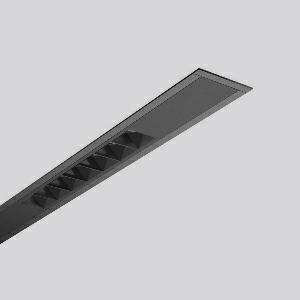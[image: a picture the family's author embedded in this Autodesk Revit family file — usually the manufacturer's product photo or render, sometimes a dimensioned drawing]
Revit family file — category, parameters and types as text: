
# Revit family: less_is_more_beamline_312467_003_1_76_66ad
name_source: partatom
category: Lighting Fixtures
units: mm (PartAtom-declared; Revit-internal decimal feet)

## family parameters
Cut with Voids When Loaded = No
Host = Face
Light Source = No
Part Type = Normal
Room Calculation Point = No
Round Connector Dimension = Use Diameter
Shared = No

## types (1)
- LESS IS MORE BEAMLINE (1 x LED Modul 940, 1100 lm, 4000)
    Apparent Load = 23 VA
    CIE Flux Codes = 100 100 100 100 100
    Color Rendering = 92
    Color Temperature = 4000
    Default Elevation = 1800 mm
    Description = Series: LESS IS MORE BEAMLINE
Linear recessed ceiling and wall luminaire for aesthetically sophisticated lighting. Luminaire with two LED light units. Housing: extruded aluminium profile, powder-coated. End cap aluminium powder-coated. LED light unit with MRS technology: Mini-Reflector-System made of metallised thermoplastic with prismatic black glare-suppressing frame for pleasant glare-free light (RUG < 10). Each LED light unit has 7 reflector elements. Wide beam light distribution. Ceiling installation with pre-assembled SBS mounting system. LED unit with integrated converter interchangeable and removable. Suitable for through-wiring. 
Colour: deep black, matt (RAL 9005)
Length: 1141 mm
Width: 71 mm
Height: 1.5 mm
Cut-out length: 1128 mm
Cut-out width: 60 mm
Recess height: 125 mm
Luminaire: recess height: 106 mm
Lamp: LED
Socket: without socket
Colour temperature: 4000K
Colour rendering index (CRI): 90
System power: 23 W
Rated luminous flux: 2200 lm
Luminous efficiency: 96 lm/W
Control gear: Converter, dimmable, DALI
Protection class: I
Type of protection: IP 20
    Height = 0 mm  [stored 0 ft]
    Lamp = 1 x LED Modul 940
    Lamp Light Flux = 1100 lm
    Lamp count = 1
    Length = 1141 mm
    Lifetime = 50000 h
    Luminous efficacy = 96 lm/W
    Manufacturer = RZB
    ModVariant = No
    Model = 312467.003.1.76
    Mounting Place = Ceiling, Wall
    Mounting Type = Recessed
    Number of Poles = 1
    OnlyDefault = Yes
    Power Factor = 1
    Product Name = LESS IS MORE BEAMLINE
    Product group = Recessed LED linear luminaires
    ProductGroupID = 407
    Protection Class = Protection class I
    Protection Degree = IP 20
    RLX_Detail_Level = 1
    RLX_Emergency_Light_Flux = 0 lm
    RLX_Emergency_Type = 0
    RLX_Emergency_Type_DB = No
    RlxData = <blob elided: 23865 chars, md5=fc73e53d>
    Socket = socket
    Standby Power = 0 W
    System Light Flux = 2200 lm
    System Power = 23 W
    Type Comments = Product without accessories
    Type Image = 312465.003.jpg
    URL = http://relux.com
    VarID = ---
    Voltage = 230 V
    Voltage Range = 220-240 V
    Weight = 0.00 kg
    Width = 71 mm

note: [stored X ft] marks values corroborated as IEEE doubles in the binary element streams (Revit-internal decimal feet)

## geometry (parser evidence)
native form markers: Blend x4, Sweep x16
no freeform markers — native parametric forms only
